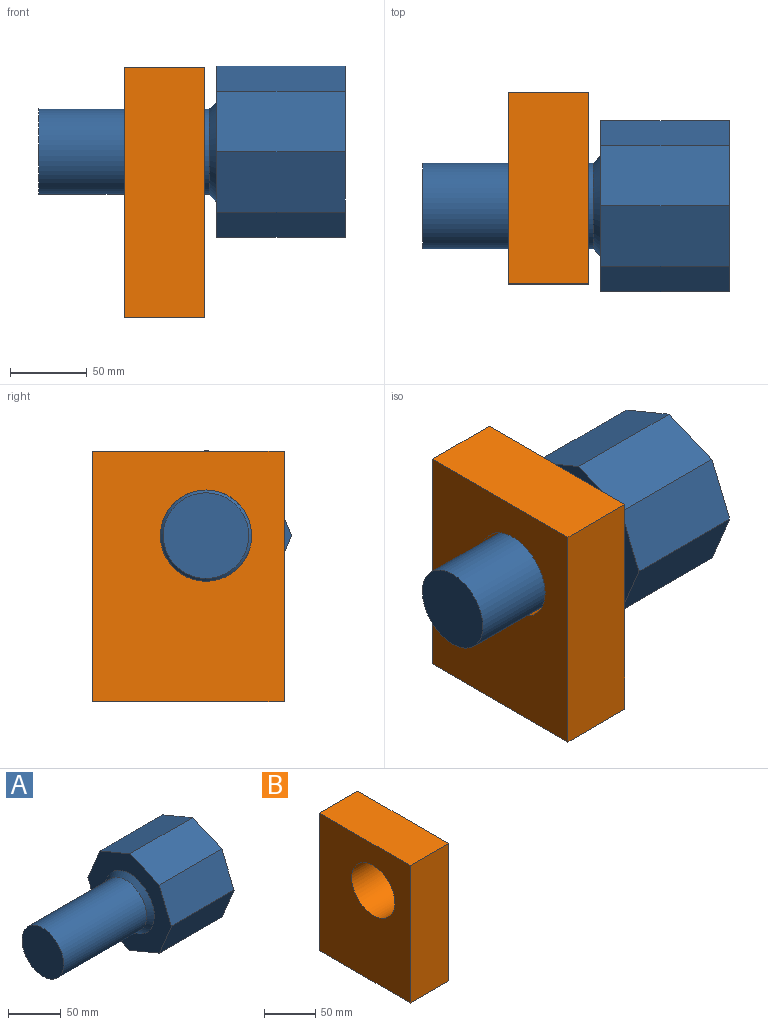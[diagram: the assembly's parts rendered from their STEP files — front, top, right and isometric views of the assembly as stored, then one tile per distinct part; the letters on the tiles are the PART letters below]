
ASSEMBLY  parts=2 mates=1
PART A: 13 faces, bbox 200x111.8x111.8 mm
  f0: plane 83.74x39.52mm, normal (0,-0.38,0.92), area 3582mm2, adj f1,f7,f8,f9
  f1: plane 83.74x39.52mm, normal (0,-0.92,0.38), area 3582mm2, adj f0,f2,f8,f9
  f2: plane 83.74x39.52mm, normal (0,-0.92,-0.38), area 3582mm2, adj f1,f3,f8,f9
  f3: plane 83.74x39.52mm, normal (0,-0.38,-0.92), area 3582mm2, adj f2,f4,f8,f9
  f4: plane 83.74x39.52mm, normal (0,0.38,-0.92), area 3582mm2, adj f3,f5,f8,f9
  f5: plane 83.74x39.52mm, normal (0,0.92,-0.38), area 3582mm2, adj f4,f6,f8,f9
  f6: plane 83.74x39.52mm, normal (0,0.92,0.38), area 3582mm2, adj f5,f7,f8,f9
  f7: plane 83.74x39.52mm, normal (0,0.38,0.92), area 3582mm2, adj f0,f6,f8,f9
  f8: plane 111.78x111.78mm, normal (1,0,0), area 8835mm2, adj f0,f1,f2,f3,f4,f5,f6,f7
  f9: plane 111.78x111.78mm, normal (-1,0,0), area 5408.7mm2, adj f0,f1,f2,f3,f4,f5,f6,f7
  f10: cylinder r=27.94mm len=111.22mm, axis (1,0,0), area 19528.2mm2, adj f11,f12
  f11: plane 55.89x55.89mm, normal (-1,0,0), area 2453.3mm2, adj f10
  f12: cone r=33.02mm half-angle=45deg, axis (1,0,0), area 1376.1mm2, adj f9,f10
PART B: 7 faces, bbox 52.6x125.2x163.8 mm
  f0: plane 163.78x125.19mm, normal (1,0,0), area 17710.9mm2, adj f1,f3,f4,f5,f6
  f1: plane 163.78x52.64mm, normal (0,1,0), area 8621.1mm2, adj f0,f2,f4,f5
  f2: plane 163.78x125.19mm, normal (-1,0,0), area 17710.9mm2, adj f1,f3,f4,f5,f6
  f3: plane 163.78x52.64mm, normal (0,-1,0), area 8621.1mm2, adj f0,f2,f4,f5
  f4: plane 125.19x52.64mm, normal (0,0,1), area 6589.8mm2, adj f0,f1,f2,f3
  f5: plane 125.19x52.64mm, normal (0,0,-1), area 6589.8mm2, adj f0,f1,f2,f3
  f6: cylinder r=29.82mm len=59.64mm, axis (-1,0,0), area 9862.1mm2, adj f0,f2
PLACE A t=(-545.3,-488.25,-659.19)mm
PLACE B t=(-580.03,-451.81,-767.86)mm
MATE revolute B.f6 <-> A.f10  axis (-1,0,0) through (-605.99,-488.25,-659.19)mm
